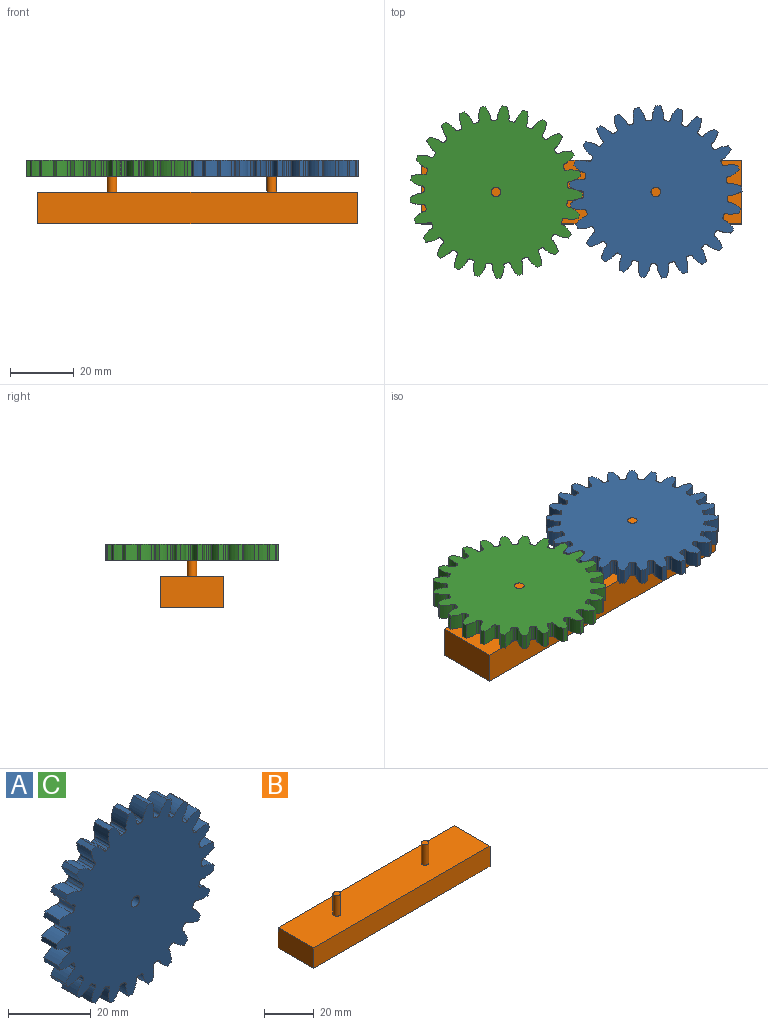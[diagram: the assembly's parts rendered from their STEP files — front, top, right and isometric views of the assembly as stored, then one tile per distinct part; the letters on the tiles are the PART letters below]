
ASSEMBLY  parts=3 mates=2
PART A: 153 faces, bbox 53.9x5.1x54 mm
  f0: extruded ~5.08x3.69mm, area 20.6mm2, adj f100,f101,f102,f103
  f1: cylinder r=22.5mm len=5.08mm, axis (0,1,0), area 3.9mm2, adj f101,f102,f103,f104
  f2: extruded ~5.08x3.69mm, area 20.6mm2, adj f3,f101,f102,f104
  f3: cylinder r=27mm len=5.08mm, axis (0,1,0), area 7.3mm2, adj f2,f4,f101,f102
  f4: extruded ~5.08x3.96mm, area 20.6mm2, adj f3,f101,f102,f105
  f5: cylinder r=22.5mm len=5.08mm, axis (0,1,0), area 3.9mm2, adj f101,f102,f105,f106
  f6: extruded ~5.08x3.18mm, area 20.6mm2, adj f7,f101,f102,f106
  f7: cylinder r=27mm len=5.08mm, axis (0,1,0), area 7.3mm2, adj f6,f8,f101,f102
  f8: extruded ~5.08x3.98mm, area 20.6mm2, adj f7,f101,f102,f107
  f9: cylinder r=22.5mm len=5.08mm, axis (0,1,0), area 3.9mm2, adj f101,f102,f107,f108
  f10: extruded ~5.08x3.14mm, area 20.6mm2, adj f11,f101,f102,f108
  f11: cylinder r=27mm len=5.08mm, axis (0,1,0), area 7.3mm2, adj f10,f12,f101,f102
  f12: extruded ~5.08x3.76mm, area 20.6mm2, adj f11,f101,f102,f109
  f13: cylinder r=22.5mm len=5.08mm, axis (0,1,0), area 3.9mm2, adj f101,f102,f109,f110
  f14: extruded ~5.08x3.66mm, area 20.6mm2, adj f15,f101,f102,f110
  f15: cylinder r=27mm len=5.08mm, axis (0,1,0), area 7.3mm2, adj f14,f16,f101,f102
  f16: extruded ~5.08x3.29mm, area 20.6mm2, adj f15,f101,f102,f111
  f17: cylinder r=22.5mm len=5.08mm, axis (0,1,0), area 3.9mm2, adj f101,f102,f111,f112
  f18: extruded ~5.08x3.95mm, area 20.6mm2, adj f19,f101,f102,f112
  f19: cylinder r=27mm len=5.08mm, axis (0,1,0), area 7.3mm2, adj f18,f20,f101,f102
  f20: extruded ~5.08x3.03mm, area 20.6mm2, adj f19,f101,f102,f113
  f21: cylinder r=22.5mm len=5.08mm, axis (0,1,0), area 3.9mm2, adj f101,f102,f113,f114
  f22: extruded ~5.08x3.99mm, area 20.6mm2, adj f23,f101,f102,f114
  f23: cylinder r=27mm len=5.08mm, axis (0,1,0), area 7.3mm2, adj f22,f24,f101,f102
  f24: extruded ~5.08x3.58mm, area 20.6mm2, adj f23,f101,f102,f115
  f25: cylinder r=22.5mm len=5.08mm, axis (0,1,0), area 3.9mm2, adj f101,f102,f115,f116
  f26: extruded ~5.08x3.78mm, area 20.6mm2, adj f27,f101,f102,f116
  f27: cylinder r=27mm len=5.08mm, axis (0,1,0), area 7.3mm2, adj f26,f28,f101,f102
  f28: extruded ~5.08x3.91mm, area 20.6mm2, adj f27,f101,f102,f117
  f29: cylinder r=22.5mm len=5.08mm, axis (0,1,0), area 3.9mm2, adj f101,f102,f117,f118
  f30: extruded ~5.08x3.33mm, area 20.6mm2, adj f31,f101,f102,f118
  f31: cylinder r=27mm len=5.08mm, axis (0,1,0), area 7.3mm2, adj f30,f32,f101,f102
  f32: extruded ~5.08x4mm, area 20.6mm2, adj f31,f101,f102,f119
  f33: cylinder r=22.5mm len=5.08mm, axis (0,1,0), area 3.9mm2, adj f101,f102,f119,f120
  f34: extruded ~5.08x2.98mm, area 20.6mm2, adj f35,f101,f102,f120
  f35: cylinder r=27mm len=5.08mm, axis (0,1,0), area 7.3mm2, adj f34,f36,f101,f102
  f36: extruded ~5.08x3.84mm, area 20.6mm2, adj f35,f101,f102,f121
  f37: cylinder r=22.5mm len=5.08mm, axis (0,1,0), area 3.9mm2, adj f101,f102,f121,f122
  f38: extruded ~5.08x3.55mm, area 20.6mm2, adj f39,f101,f102,f122
  f39: cylinder r=27mm len=5.08mm, axis (0,1,0), area 7.3mm2, adj f38,f40,f101,f102
  f40: extruded ~5.08x3.43mm, area 20.6mm2, adj f39,f101,f102,f123
  f41: cylinder r=22.5mm len=5.08mm, axis (0,1,0), area 3.9mm2, adj f101,f102,f123,f124
  f42: extruded ~5.08x3.9mm, area 20.6mm2, adj f43,f101,f102,f124
  f43: cylinder r=27mm len=5.08mm, axis (0,1,0), area 7.3mm2, adj f42,f44,f101,f102
  f44: extruded ~5.08x2.85mm, area 20.6mm2, adj f43,f101,f102,f125
  f45: cylinder r=22.5mm len=5.08mm, axis (0,1,0), area 3.9mm2, adj f101,f102,f125,f126
  f46: extruded ~5.08x4mm, area 20.6mm2, adj f47,f101,f102,f126
  f47: cylinder r=27mm len=5.08mm, axis (0,1,0), area 7.3mm2, adj f46,f48,f101,f102
  f48: extruded ~5.08x3.46mm, area 20.6mm2, adj f47,f101,f102,f127
  f49: cylinder r=22.5mm len=5.08mm, axis (0,1,0), area 3.9mm2, adj f101,f102,f127,f128
  f50: extruded ~5.08x3.85mm, area 20.6mm2, adj f51,f101,f102,f128
  f51: cylinder r=27mm len=5.08mm, axis (0,1,0), area 7.3mm2, adj f50,f52,f101,f102
  f52: extruded ~5.08x3.85mm, area 20.6mm2, adj f51,f101,f102,f129
  f53: cylinder r=22.5mm len=5.08mm, axis (0,1,0), area 3.9mm2, adj f101,f102,f129,f130
  f54: extruded ~5.08x3.46mm, area 20.6mm2, adj f55,f101,f102,f130
  f55: cylinder r=27mm len=5.08mm, axis (0,1,0), area 7.3mm2, adj f54,f56,f101,f102
  f56: extruded ~5.08x4mm, area 20.6mm2, adj f55,f101,f102,f131
  f57: cylinder r=22.5mm len=5.08mm, axis (0,1,0), area 3.9mm2, adj f101,f102,f131,f132
  f58: extruded ~5.08x2.85mm, area 20.6mm2, adj f59,f101,f102,f132
  f59: cylinder r=27mm len=5.08mm, axis (0,1,0), area 7.3mm2, adj f58,f60,f101,f102
  f60: extruded ~5.08x3.9mm, area 20.6mm2, adj f59,f101,f102,f133
  f61: cylinder r=22.5mm len=5.08mm, axis (0,1,0), area 3.9mm2, adj f101,f102,f133,f134
  f62: extruded ~5.08x3.43mm, area 20.6mm2, adj f63,f101,f102,f134
  f63: cylinder r=27mm len=5.08mm, axis (0,1,0), area 7.3mm2, adj f62,f64,f101,f102
  f64: extruded ~5.08x3.55mm, area 20.6mm2, adj f63,f101,f102,f135
  f65: cylinder r=22.5mm len=5.08mm, axis (0,1,0), area 3.9mm2, adj f101,f102,f135,f136
  f66: extruded ~5.08x3.84mm, area 20.6mm2, adj f67,f101,f102,f136
  f67: cylinder r=27mm len=5.08mm, axis (0,1,0), area 7.3mm2, adj f66,f68,f101,f102
  f68: extruded ~5.08x2.98mm, area 20.6mm2, adj f67,f101,f102,f137
  f69: cylinder r=22.5mm len=5.08mm, axis (0,1,0), area 3.9mm2, adj f101,f102,f137,f138
  f70: extruded ~5.08x4mm, area 20.6mm2, adj f71,f101,f102,f138
  f71: cylinder r=27mm len=5.08mm, axis (0,1,0), area 7.3mm2, adj f70,f72,f101,f102
  f72: extruded ~5.08x3.33mm, area 20.6mm2, adj f71,f101,f102,f139
  f73: cylinder r=22.5mm len=5.08mm, axis (0,1,0), area 3.9mm2, adj f101,f102,f139,f140
  f74: extruded ~5.08x3.91mm, area 20.6mm2, adj f75,f101,f102,f140
  f75: cylinder r=27mm len=5.08mm, axis (0,1,0), area 7.3mm2, adj f74,f76,f101,f102
  f76: extruded ~5.08x3.78mm, area 20.6mm2, adj f75,f101,f102,f141
  f77: cylinder r=22.5mm len=5.08mm, axis (0,1,0), area 3.9mm2, adj f101,f102,f141,f142
  f78: extruded ~5.08x3.58mm, area 20.6mm2, adj f79,f101,f102,f142
  f79: cylinder r=27mm len=5.08mm, axis (0,1,0), area 7.3mm2, adj f78,f80,f101,f102
  f80: extruded ~5.08x3.99mm, area 20.6mm2, adj f79,f101,f102,f143
  f81: cylinder r=22.5mm len=5.08mm, axis (0,1,0), area 3.9mm2, adj f101,f102,f143,f144
  f82: extruded ~5.08x3.03mm, area 20.6mm2, adj f83,f101,f102,f144
  f83: cylinder r=27mm len=5.08mm, axis (0,1,0), area 7.3mm2, adj f82,f84,f101,f102
  f84: extruded ~5.08x3.95mm, area 20.6mm2, adj f83,f101,f102,f145
  f85: cylinder r=22.5mm len=5.08mm, axis (0,1,0), area 3.9mm2, adj f101,f102,f145,f146
  f86: extruded ~5.08x3.29mm, area 20.6mm2, adj f87,f101,f102,f146
  f87: cylinder r=27mm len=5.08mm, axis (0,1,0), area 7.3mm2, adj f86,f88,f101,f102
  f88: extruded ~5.08x3.66mm, area 20.6mm2, adj f87,f101,f102,f147
  f89: cylinder r=22.5mm len=5.08mm, axis (0,1,0), area 3.9mm2, adj f101,f102,f147,f148
  f90: extruded ~5.08x3.76mm, area 20.6mm2, adj f91,f101,f102,f148
  f91: cylinder r=27mm len=5.08mm, axis (0,1,0), area 7.3mm2, adj f90,f92,f101,f102
  f92: extruded ~5.08x3.14mm, area 20.6mm2, adj f91,f101,f102,f149
  f93: cylinder r=22.5mm len=5.08mm, axis (0,1,0), area 3.9mm2, adj f101,f102,f149,f150
  f94: extruded ~5.08x3.98mm, area 20.6mm2, adj f95,f101,f102,f150
  f95: cylinder r=27mm len=5.08mm, axis (0,1,0), area 7.3mm2, adj f94,f96,f101,f102
  f96: extruded ~5.08x3.18mm, area 20.6mm2, adj f95,f101,f102,f151
  f97: cylinder r=22.5mm len=5.08mm, axis (0,1,0), area 3.9mm2, adj f101,f102,f151,f152
  f98: extruded ~5.08x3.96mm, area 20.6mm2, adj f100,f101,f102,f152
  f99: cylinder r=1.5mm len=5.08mm, axis (0,1,0), area 47.9mm2, adj f101,f102
  f100: cylinder r=27mm len=5.08mm, axis (0,1,0), area 7.3mm2, adj f0,f98,f101,f102
  f101: plane 53.98x53.87mm, normal (0,-1,0), area 1926.9mm2, adj f0,f1,f2,f3,f4,f5,f6,f7
  f102: plane 53.98x53.87mm, normal (0,1,0), area 1926.9mm2, adj f0,f1,f2,f3,f4,f5,f6,f7
  f103: cylinder r=0.72mm len=5.08mm, axis (0,1,0), area 5.6mm2, adj f0,f1,f101,f102
  f104: cylinder r=0.72mm len=5.08mm, axis (0,1,0), area 5.6mm2, adj f1,f2,f101,f102
  f105: cylinder r=0.72mm len=5.08mm, axis (0,1,0), area 5.6mm2, adj f4,f5,f101,f102
  f106: cylinder r=0.72mm len=5.08mm, axis (0,1,0), area 5.6mm2, adj f5,f6,f101,f102
  f107: cylinder r=0.72mm len=5.08mm, axis (0,1,0), area 5.6mm2, adj f8,f9,f101,f102
  f108: cylinder r=0.72mm len=5.08mm, axis (0,1,0), area 5.6mm2, adj f9,f10,f101,f102
  f109: cylinder r=0.72mm len=5.08mm, axis (0,1,0), area 5.6mm2, adj f12,f13,f101,f102
  f110: cylinder r=0.72mm len=5.08mm, axis (0,1,0), area 5.6mm2, adj f13,f14,f101,f102
  f111: cylinder r=0.72mm len=5.08mm, axis (0,1,0), area 5.6mm2, adj f16,f17,f101,f102
  f112: cylinder r=0.72mm len=5.08mm, axis (0,1,0), area 5.6mm2, adj f17,f18,f101,f102
  f113: cylinder r=0.72mm len=5.08mm, axis (0,1,0), area 5.6mm2, adj f20,f21,f101,f102
  f114: cylinder r=0.72mm len=5.08mm, axis (0,1,0), area 5.6mm2, adj f21,f22,f101,f102
  f115: cylinder r=0.72mm len=5.08mm, axis (0,1,0), area 5.6mm2, adj f24,f25,f101,f102
  f116: cylinder r=0.72mm len=5.08mm, axis (0,1,0), area 5.6mm2, adj f25,f26,f101,f102
  f117: cylinder r=0.72mm len=5.08mm, axis (0,1,0), area 5.6mm2, adj f28,f29,f101,f102
  f118: cylinder r=0.72mm len=5.08mm, axis (0,1,0), area 5.6mm2, adj f29,f30,f101,f102
  f119: cylinder r=0.72mm len=5.08mm, axis (0,1,0), area 5.6mm2, adj f32,f33,f101,f102
  f120: cylinder r=0.72mm len=5.08mm, axis (0,1,0), area 5.6mm2, adj f33,f34,f101,f102
  f121: cylinder r=0.72mm len=5.08mm, axis (0,1,0), area 5.6mm2, adj f36,f37,f101,f102
  f122: cylinder r=0.72mm len=5.08mm, axis (0,1,0), area 5.6mm2, adj f37,f38,f101,f102
  f123: cylinder r=0.72mm len=5.08mm, axis (0,1,0), area 5.6mm2, adj f40,f41,f101,f102
  f124: cylinder r=0.72mm len=5.08mm, axis (0,1,0), area 5.6mm2, adj f41,f42,f101,f102
  f125: cylinder r=0.72mm len=5.08mm, axis (0,1,0), area 5.6mm2, adj f44,f45,f101,f102
  f126: cylinder r=0.72mm len=5.08mm, axis (0,1,0), area 5.6mm2, adj f45,f46,f101,f102
  f127: cylinder r=0.72mm len=5.08mm, axis (0,1,0), area 5.6mm2, adj f48,f49,f101,f102
  f128: cylinder r=0.72mm len=5.08mm, axis (0,1,0), area 5.6mm2, adj f49,f50,f101,f102
  f129: cylinder r=0.72mm len=5.08mm, axis (0,1,0), area 5.6mm2, adj f52,f53,f101,f102
  f130: cylinder r=0.72mm len=5.08mm, axis (0,1,0), area 5.6mm2, adj f53,f54,f101,f102
  f131: cylinder r=0.72mm len=5.08mm, axis (0,1,0), area 5.6mm2, adj f56,f57,f101,f102
  f132: cylinder r=0.72mm len=5.08mm, axis (0,1,0), area 5.6mm2, adj f57,f58,f101,f102
  f133: cylinder r=0.72mm len=5.08mm, axis (0,1,0), area 5.6mm2, adj f60,f61,f101,f102
  f134: cylinder r=0.72mm len=5.08mm, axis (0,1,0), area 5.6mm2, adj f61,f62,f101,f102
  f135: cylinder r=0.72mm len=5.08mm, axis (0,1,0), area 5.6mm2, adj f64,f65,f101,f102
  f136: cylinder r=0.72mm len=5.08mm, axis (0,1,0), area 5.6mm2, adj f65,f66,f101,f102
  f137: cylinder r=0.72mm len=5.08mm, axis (0,1,0), area 5.6mm2, adj f68,f69,f101,f102
  f138: cylinder r=0.72mm len=5.08mm, axis (0,1,0), area 5.6mm2, adj f69,f70,f101,f102
  f139: cylinder r=0.72mm len=5.08mm, axis (0,1,0), area 5.6mm2, adj f72,f73,f101,f102
  f140: cylinder r=0.72mm len=5.08mm, axis (0,1,0), area 5.6mm2, adj f73,f74,f101,f102
  f141: cylinder r=0.72mm len=5.08mm, axis (0,1,0), area 5.6mm2, adj f76,f77,f101,f102
  f142: cylinder r=0.72mm len=5.08mm, axis (0,1,0), area 5.6mm2, adj f77,f78,f101,f102
  f143: cylinder r=0.72mm len=5.08mm, axis (0,1,0), area 5.6mm2, adj f80,f81,f101,f102
  f144: cylinder r=0.72mm len=5.08mm, axis (0,1,0), area 5.6mm2, adj f81,f82,f101,f102
  f145: cylinder r=0.72mm len=5.08mm, axis (0,1,0), area 5.6mm2, adj f84,f85,f101,f102
  f146: cylinder r=0.72mm len=5.08mm, axis (0,1,0), area 5.6mm2, adj f85,f86,f101,f102
  f147: cylinder r=0.72mm len=5.08mm, axis (0,1,0), area 5.6mm2, adj f88,f89,f101,f102
  f148: cylinder r=0.72mm len=5.08mm, axis (0,1,0), area 5.6mm2, adj f89,f90,f101,f102
  f149: cylinder r=0.72mm len=5.08mm, axis (0,1,0), area 5.6mm2, adj f92,f93,f101,f102
  f150: cylinder r=0.72mm len=5.08mm, axis (0,1,0), area 5.6mm2, adj f93,f94,f101,f102
  f151: cylinder r=0.72mm len=5.08mm, axis (0,1,0), area 5.6mm2, adj f96,f97,f101,f102
  f152: cylinder r=0.72mm len=5.08mm, axis (0,1,0), area 5.6mm2, adj f97,f98,f101,f102
PART B: 10 faces, bbox 100x20x20 mm
  f0: plane 20x10mm, normal (1,0,0), area 200mm2, adj f1,f3,f4,f5
  f1: plane 100x10mm, normal (0,1,0), area 1000mm2, adj f0,f2,f4,f5
  f2: plane 20x10mm, normal (-1,0,0), area 200mm2, adj f1,f3,f4,f5
  f3: plane 100x10mm, normal (0,-1,0), area 1000mm2, adj f0,f2,f4,f5
  f4: plane 100x20mm, normal (0,0,1), area 1985.9mm2, adj f0,f1,f2,f3,f6,f8
  f5: plane 100x20mm, normal (0,0,-1), area 2000mm2, adj f0,f1,f2,f3
  f6: cylinder r=1.5mm len=10mm, axis (0,0,-1), area 94.2mm2, adj f4,f7
  f7: plane 3x3mm, normal (0,0,1), area 7.1mm2, adj f6
  f8: cylinder r=1.5mm len=10mm, axis (0,0,-1), area 94.2mm2, adj f4,f9
  f9: plane 3x3mm, normal (0,0,1), area 7.1mm2, adj f8
PART C: same geometry as A
PLACE A rot(axis=(-0.44,-0.63,0.63),132.1deg) t=(-41.67,-36.84,-6.79)mm
PLACE B t=(-64.92,-36.84,-21.71)mm fixed
PLACE C rot(axis=(-0.44,0.63,-0.63),132.1deg) t=(-91.67,-36.84,-6.79)mm
MATE revolute C.f3 <-> B.f6  axis (0,0,1) through (-91.67,-36.84,-1.71)mm
MATE revolute A.f3 <-> B.f8  axis (0,0,1) through (-41.67,-36.84,-1.71)mm
